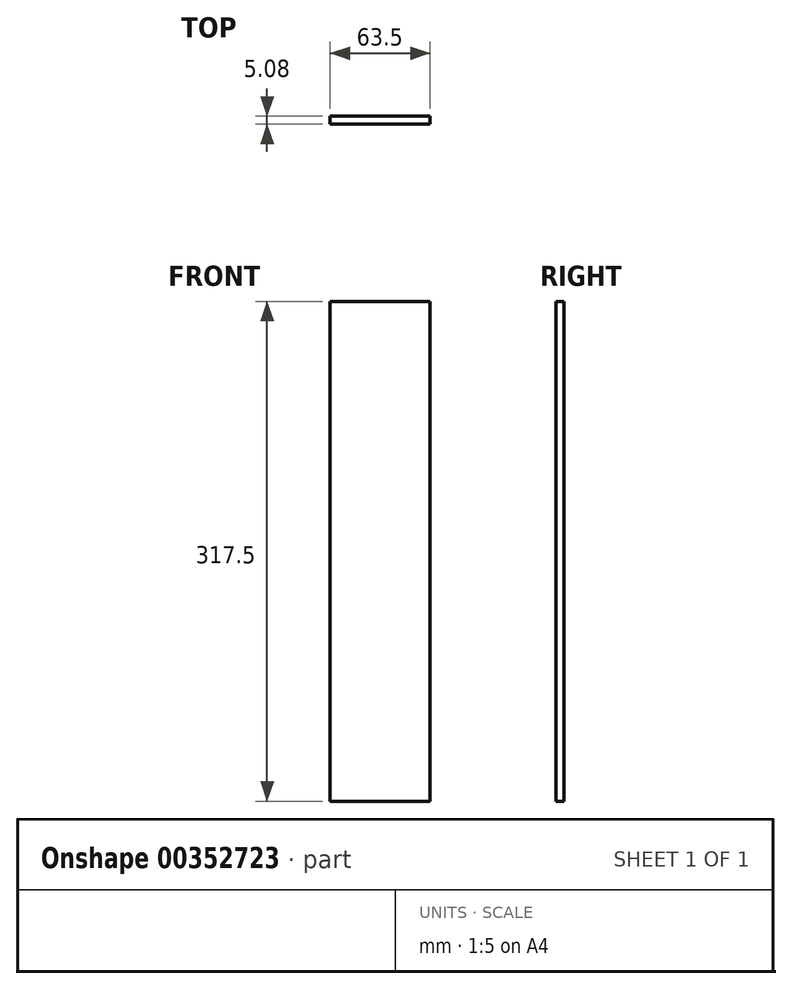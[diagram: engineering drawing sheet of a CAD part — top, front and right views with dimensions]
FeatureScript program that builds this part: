
annotation { "Feature Type Name" : "Feature", "Feature Type Description" : "" }
export const myFeature = defineFeature(function(context is Context, id is Id, definition is map)
    precondition{}
    {
        {
            var Q0;
            Q0=qCreatedBy(makeId("Front.planeOp"),FACE);
            var sketch = newSketch(context, id + "F0", { "sketchPlane" : qUnion([Q0])});
            skLineSegment(sketch, "E0.bottom", {"start": v(31.75, -158.75) * mm, "end": v(-31.75, -158.75) * mm});
            skLineSegment(sketch, "E0.top", {"start": v(31.75, 158.75) * mm, "end": v(-31.75, 158.75) * mm});
            skLineSegment(sketch, "E0.left", {"start": v(31.75, -158.75) * mm, "end": v(31.75, 158.75) * mm});
            skLineSegment(sketch, "E0.right", {"start": v(-31.75, -158.75) * mm, "end": v(-31.75, 158.75) * mm});
            skPoint(sketch, "E0.middle", {"position": v(0, 0) * mm});
            skSolve(sketch);
        }
        {
            var Q0;
            Q0=makeQuery(id+"F0.imprint","IMPRINT",FACE,{"disambiguationData":[TD([[makeQuery(id+"F0.imprint","IMPRINT",EDGE,{"derivedFrom":sQuery(id+"F0.wireOp",EDGE,"E0.bottom")}),-1.0]])]});
            extrude(context, id + "F1", {"entities" : qUnion([Q0]), "depth" : 5.08 * mm});
        }
    });
